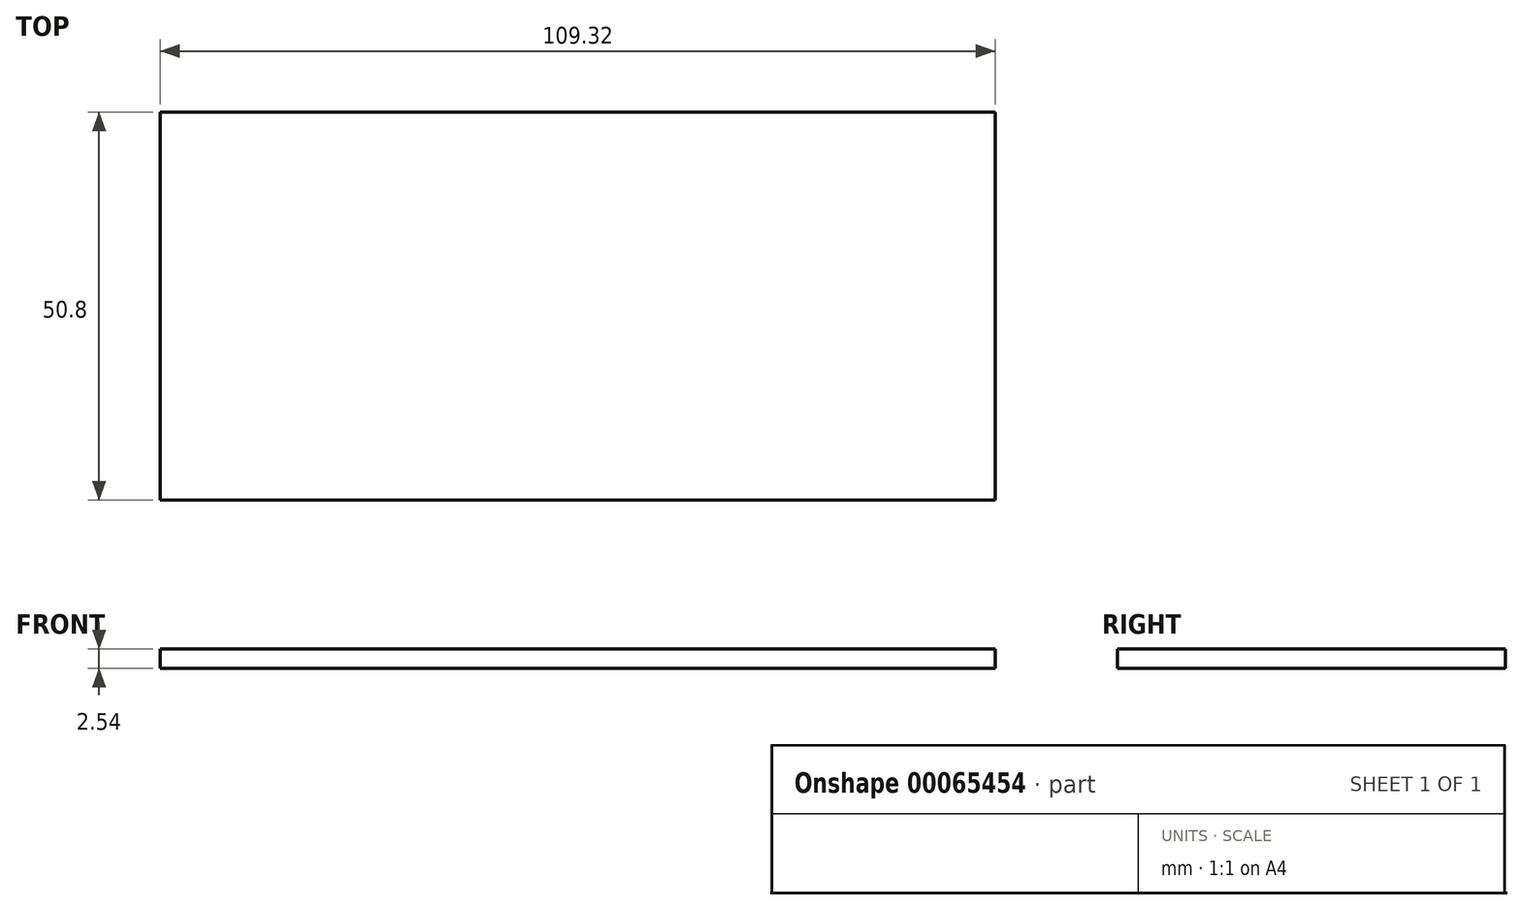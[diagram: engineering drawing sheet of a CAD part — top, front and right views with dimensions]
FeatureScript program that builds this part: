
annotation { "Feature Type Name" : "Feature", "Feature Type Description" : "" }
export const myFeature = defineFeature(function(context is Context, id is Id, definition is map)
    precondition{}
    {
        {
            var Q0;
            Q0=qCreatedBy(makeId("Front.planeOp"),FACE);
            var sketch = newSketch(context, id + "F0", { "sketchPlane" : qUnion([Q0])});
            skLineSegment(sketch, "E0.bottom", {"start": v(-21.24, 0.22) * mm, "end": v(88.08, 0.22) * mm});
            skLineSegment(sketch, "E0.top", {"start": v(-21.24, -2.32) * mm, "end": v(88.08, -2.32) * mm});
            skLineSegment(sketch, "E0.left", {"start": v(-21.24, 0.22) * mm, "end": v(-21.24, -2.32) * mm});
            skLineSegment(sketch, "E0.right", {"start": v(88.08, 0.22) * mm, "end": v(88.08, -2.32) * mm});
            skSolve(sketch);
        }
        {
            var Q0;
            Q0 = qSketchRegion(id + "F0", true);
            extrude(context, id + "F1", {"entities" : qUnion([Q0]), "depth" : 50.8 * mm});
        }
    });
